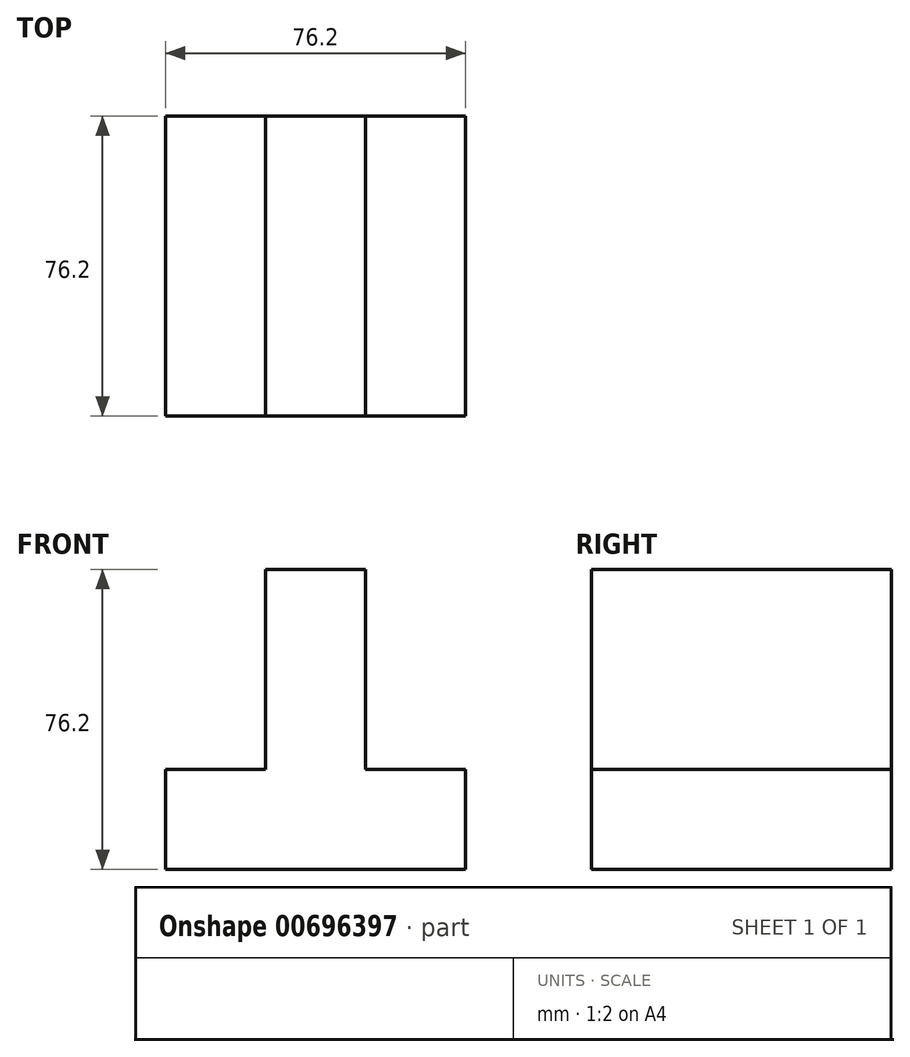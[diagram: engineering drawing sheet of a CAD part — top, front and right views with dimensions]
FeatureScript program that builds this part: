
annotation { "Feature Type Name" : "Feature", "Feature Type Description" : "" }
export const myFeature = defineFeature(function(context is Context, id is Id, definition is map)
    precondition{}
    {
        {
            var Q0;
            Q0=qCreatedBy(makeId("Front.planeOp"),FACE);
            var sketch = newSketch(context, id + "F0", { "sketchPlane" : qUnion([Q0])});
            skLineSegment(sketch, "E0", {"start": v(0, 0) * mm, "end": v(-76.2, 0) * mm});
            skLineSegment(sketch, "E1", {"start": v(-76.2, 0) * mm, "end": v(-76.2, 25.4) * mm});
            skLineSegment(sketch, "E2", {"start": v(0, 0) * mm, "end": v(0, 25.4) * mm});
            skLineSegment(sketch, "E3", {"start": v(0, 25.4) * mm, "end": v(-25.4, 25.4) * mm});
            skLineSegment(sketch, "E4", {"start": v(-25.4, 25.4) * mm, "end": v(-25.4, 76.2) * mm});
            skLineSegment(sketch, "E5", {"start": v(-25.4, 76.2) * mm, "end": v(-50.8, 76.2) * mm});
            skLineSegment(sketch, "E6", {"start": v(-50.8, 76.2) * mm, "end": v(-50.8, 25.4) * mm});
            skLineSegment(sketch, "E7", {"start": v(-50.8, 25.4) * mm, "end": v(-76.2, 25.4) * mm});
            skSolve(sketch);
        }
        {
            var Q0;
            Q0=makeQuery(id+"F0.imprint","IMPRINT",FACE,{"disambiguationData":[TD([[makeQuery(id+"F0.imprint","IMPRINT",EDGE,{"derivedFrom":sQuery(id+"F0.wireOp",EDGE,"E0")}),-1.0]])]});
            extrude(context, id + "F1", {"entities" : qUnion([Q0]), "depth" : 76.2 * mm, "offsetDistance" : 25.4 * mm});
        }
    });
